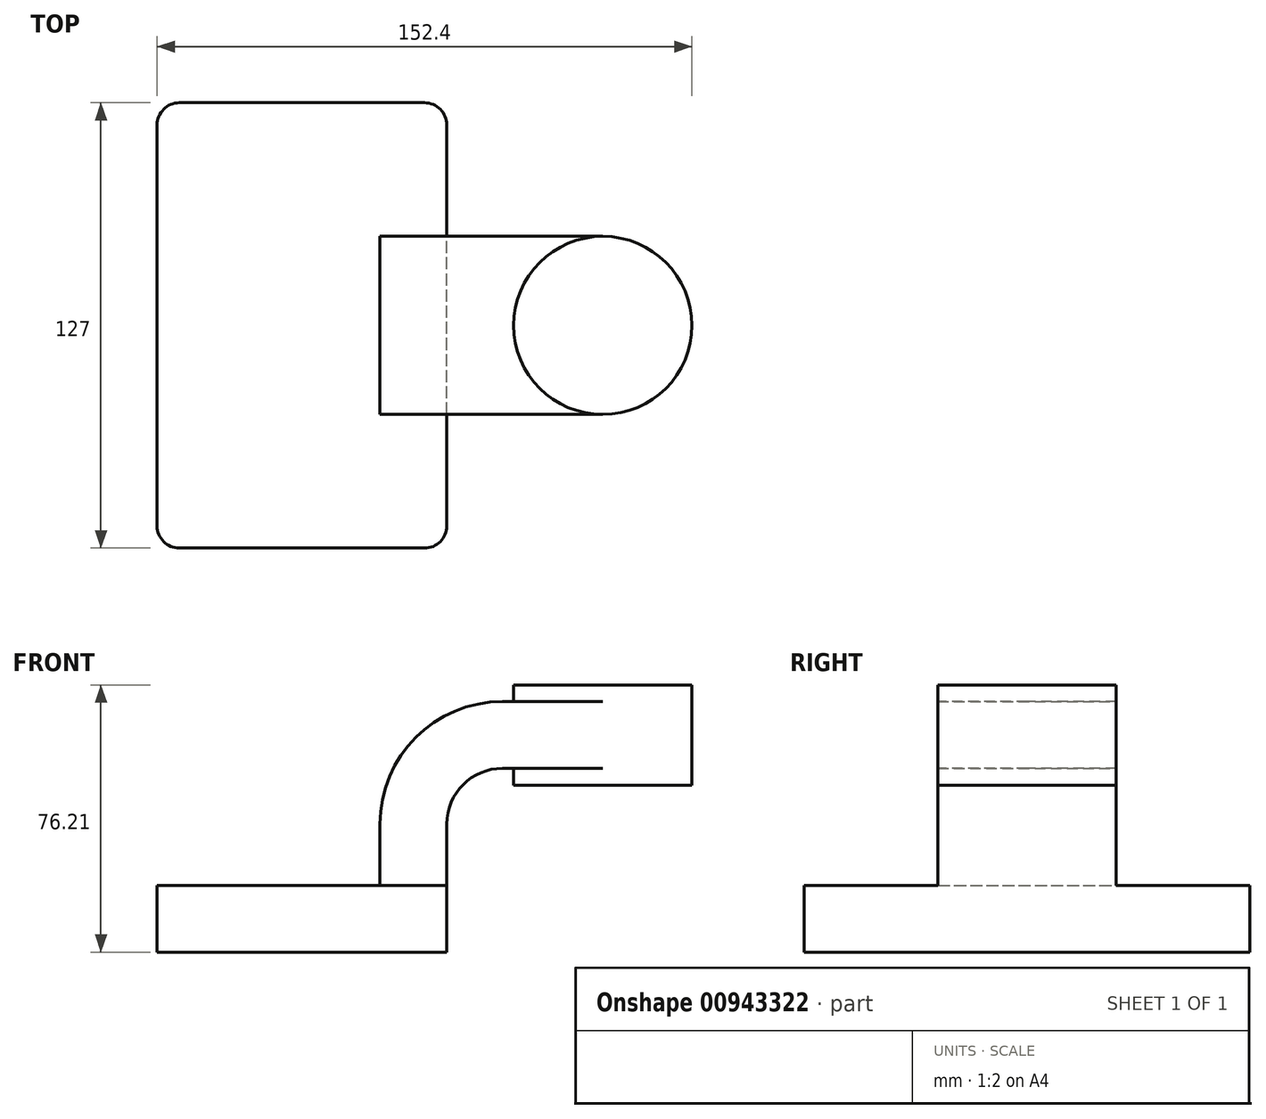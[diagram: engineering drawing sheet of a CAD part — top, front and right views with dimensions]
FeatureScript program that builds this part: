
annotation { "Feature Type Name" : "Feature", "Feature Type Description" : "" }
export const myFeature = defineFeature(function(context is Context, id is Id, definition is map)
    precondition{}
    {
        {
            var Q0;
            Q0=qCreatedBy(makeId("Front.planeOp"),FACE);
            var sketch = newSketch(context, id + "F0", { "sketchPlane" : qUnion([Q0])});
            skLineSegment(sketch, "E0.bottom", {"start": v(-41.28, 9.52) * mm, "end": v(41.27, 9.53) * mm});
            skLineSegment(sketch, "E0.top", {"start": v(-41.28, -9.53) * mm, "end": v(41.28, -9.53) * mm});
            skLineSegment(sketch, "E0.left", {"start": v(-41.28, 9.52) * mm, "end": v(-41.28, -9.53) * mm});
            skLineSegment(sketch, "E0.right", {"start": v(41.27, 9.53) * mm, "end": v(41.28, -9.52) * mm});
            skPoint(sketch, "E0.middle", {"position": v(0, 0) * mm});
            skPoint(sketch, "E1.middle", {"position": v(85.73, 42.88) * mm});
            skLineSegment(sketch, "E2", {"start": v(41.27, 9.53) * mm, "end": v(41.27, 27) * mm});
            skArc(sketch, "E3", {"start": v(41.28, 27) * mm, "mid": v(45.92, 38.23) * mm, "end": v(57.15, 42.88) * mm});
            skLineSegment(sketch, "E4", {"start": v(57.15, 42.88) * mm, "end": v(85.73, 42.88) * mm});
            skLineSegment(sketch, "E5.bottom", {"start": v(111.12, 66.67) * mm, "end": v(60.32, 66.67) * mm});
            skLineSegment(sketch, "E5.top", {"start": v(111.12, 38.1) * mm, "end": v(60.32, 38.1) * mm});
            skLineSegment(sketch, "E5.left", {"start": v(111.12, 66.68) * mm, "end": v(111.12, 38.1) * mm});
            skLineSegment(sketch, "E5.right", {"start": v(60.32, 66.68) * mm, "end": v(60.32, 38.1) * mm});
            skPoint(sketch, "E5.middle", {"position": v(85.72, 52.39) * mm});
            skLineSegment(sketch, "E6.0", {"start": v(57.15, 61.93) * mm, "end": v(85.73, 61.93) * mm});
            skArc(sketch, "E6.1", {"start": v(22.23, 27) * mm, "mid": v(32.45, 51.7) * mm, "end": v(57.15, 61.93) * mm});
            skLineSegment(sketch, "E6.2", {"start": v(22.22, 9.53) * mm, "end": v(22.22, 27) * mm});
            skLineSegment(sketch, "E7", {"start": v(85.72, 38.1) * mm, "end": v(85.72, 66.67) * mm});
            skFitSpline(sketch, "E8", {"points": [v(-41.28, 9.52) * mm, v(57.15, 61.93) * mm], "startDerivative": vector(34.83, 88.56) * mm, "endDerivative": vector(124.68, -4.12) * mm});
            skSolve(sketch);
        }
        {
            var Q0;
            Q0=makeQuery(id+"F0.imprint","IMPRINT",FACE,{"disambiguationData":[TD([[makeQuery(id+"F0.imprint","IMPRINT",EDGE,{"derivedFrom":sQuery(id+"F0.wireOp",EDGE,"E0.top")}),1.0]])]});
            extrude(context, id + "F1", {"entities" : qUnion([Q0]), "endBound" : BoundingType.SYMMETRIC, "depth" : 127 * mm, "offsetDistance" : 25.4 * mm});
        }
        {
            var Q0;
            {var subQ4=sQuery(id+"F0.wireOp",EDGE,"E2");Q0=makeQuery(id+"F0.imprint","IMPRINT",FACE,{"disambiguationData":[TD([[makeQuery(id+"F0.imprint","IMPRINT",EDGE,{"derivedFrom":subQ4}),1.0]])]});}
            var Q1;
            {var subQ0=sQuery(id+"F0.wireOp",EDGE,"E7");var subQ1=sQuery(id+"F0.wireOp",EDGE,"E4");var subQ2=makeQuery(id+"F0.imprint","INTERSECT",VERTEX,{"derivedFrom":[subQ1,subQ0]});Q1=makeQuery(id+"F0.imprint","IMPRINT",FACE,{"disambiguationData":[TD([[makeQuery(id+"F0.imprint","IMPRINT",EDGE,{"disambiguationData":[TD([[subQ2,1.0]])],"derivedFrom":subQ1}),1.0]])]});}
            extrude(context, id + "F2", {"entities" : qUnion([Q0, Q1]), "operationType" : NewBodyOperationType.ADD, "endBound" : BoundingType.SYMMETRIC, "depth" : 50.8 * mm, "offsetDistance" : 25.4 * mm});
        }
        {
            var Q0;
            Q0=makeQuery(id+"F0.imprint","IMPRINT",FACE,{"disambiguationData":[TD([[makeQuery(id+"F0.imprint","IMPRINT",EDGE,{"derivedFrom":sQuery(id+"F0.wireOp",EDGE,"E6.1")}),1.0]])]});
            extrude(context, id + "F3", {"entities" : qUnion([Q0]), "operationType" : NewBodyOperationType.ADD, "endBound" : BoundingType.SYMMETRIC, "depth" : 15.88 * mm, "offsetDistance" : 25.4 * mm});
        }
        {
            var Q0;
            {var subQ0=sQuery(id+"F0.wireOp",EDGE,"E5.left");Q0=makeQuery(id+"F0.imprint","IMPRINT",FACE,{"disambiguationData":[TD([[makeQuery(id+"F0.imprint","IMPRINT",EDGE,{"derivedFrom":subQ0}),-1.0]])]});}
            var Q1;
            Q1=sQuery(id+"F0.wireOp",EDGE,"E7");
            revolve(context, id + "F4", {"operationType" : NewBodyOperationType.ADD, "surfaceOperationType" : NewSurfaceOperationType.NEW, "entities" : qUnion([Q0]), "axis" : qUnion([Q1]), "revolveType" : RevolveType.FULL});
        }
        {
            var Q0;
            Q0=makeQuery(id+"F1.opExtrude","CAP_EDGE",EDGE,{"disambiguationData":[OSD([sQuery(id+"F0.wireOp",EDGE,"E0.left")])],"isStart":false});
            var Q1;
            Q1=makeQuery(id+"F1.opExtrude","CAP_EDGE",EDGE,{"disambiguationData":[OSD([sQuery(id+"F0.wireOp",EDGE,"E0.right")])],"isStart":false});
            var Q2;
            Q2=makeQuery(id+"F1.opExtrude","CAP_EDGE",EDGE,{"disambiguationData":[OSD([sQuery(id+"F0.wireOp",EDGE,"E0.left")])],"isStart":true});
            var Q3;
            Q3=makeQuery(id+"F1.opExtrude","CAP_EDGE",EDGE,{"disambiguationData":[OSD([sQuery(id+"F0.wireOp",EDGE,"E0.right")])],"isStart":true});
            fillet(context, id + "F5", {"entities" : qUnion([Q0, Q1, Q2, Q3]), "radius" : 6.35 * mm, "tangentPropagation" : true, "allowEdgeOverflow" : false});
        }
    });
